# Revit family: Timber-Column
name_source: partatom
category: Structural Columns
revit_build: Autodesk Revit Architecture 2012 (Build: 20110210_1515)
units: mm (PartAtom-declared; Revit-internal decimal feet)

## types (56) — shared parameters
Assembly Code = B10

## per-type parameters (varying)
| type | A | b | d |
| 5x5 | 20.25 in² | 0' - 4 1/2" | 0' - 4 1/2" |
| 6x6 | 30.25 in² | 0' - 5 1/2" | 0' - 5 1/2" |
| 6x8 | 41.25 in² | 0' - 5 1/2" | 0' - 7 1/2" |
| 6x10 | 52.25 in² | 0' - 5 1/2" | 0' - 9 1/2" |
| 6x12 | 63.25 in² | 0' - 5 1/2" | 0' - 11 1/2" |
| 6x14 | 74.25 in² | 0' - 5 1/2" | 1' - 1 1/2" |
| 6x16 | 85.25 in² | 0' - 5 1/2" | 1' - 3 1/2" |
| 6x18 | 96.25 in² | 0' - 5 1/2" | 1' - 5 1/2" |
| 6x20 | 107.3 in² | 0' - 5 1/2" | 1' - 7 1/2" |
| 6x22 | 118.3 in² | 0' - 5 1/2" | 1' - 9 1/2" |
| 6x24 | 129.3 in² | 0' - 5 1/2" | 1' - 11 1/2" |
| 8x8 | 56.25 in² | 0' - 7 1/2" | 0' - 7 1/2" |
| 8x10 | 71.25 in² | 0' - 7 1/2" | 0' - 9 1/2" |
| 8x12 | 86.25 in² | 0' - 7 1/2" | 0' - 11 1/2" |
| 8x14 | 101.3 in² | 0' - 7 1/2" | 1' - 1 1/2" |
| 8x16 | 116.3 in² | 0' - 7 1/2" | 1' - 3 1/2" |
| 8x18 | 131.3 in² | 0' - 7 1/2" | 1' - 5 1/2" |
| 8x20 | 146.3 in² | 0' - 7 1/2" | 1' - 7 1/2" |
| 8x22 | 161.3 in² | 0' - 7 1/2" | 1' - 9 1/2" |
| 8x24 | 176.3 in² | 0' - 7 1/2" | 1' - 11 1/2" |
| 10x10 | 90.25 in² | 0' - 9 1/2" | 0' - 9 1/2" |
| 10x12 | 109.3 in² | 0' - 9 1/2" | 0' - 11 1/2" |
| 10x14 | 128.3 in² | 0' - 9 1/2" | 1' - 1 1/2" |
| 10x16 | 147.3 in² | 0' - 9 1/2" | 1' - 3 1/2" |
| 10x18 | 166.3 in² | 0' - 9 1/2" | 1' - 5 1/2" |
| 10x20 | 185.3 in² | 0' - 9 1/2" | 1' - 7 1/2" |
| 10x22 | 204.3 in² | 0' - 9 1/2" | 1' - 9 1/2" |
| 10x24 | 223.3 in² | 0' - 9 1/2" | 1' - 11 1/2" |
| 12x12 | 132.3 in² | 0' - 11 1/2" | 0' - 11 1/2" |
| 12x14 | 155.3 in² | 0' - 11 1/2" | 1' - 1 1/2" |
| 12x16 | 178.3 in² | 0' - 11 1/2" | 1' - 3 1/2" |
| 12x18 | 201.3 in² | 0' - 11 1/2" | 1' - 5 1/2" |
| 12x20 | 224.3 in² | 0' - 11 1/2" | 1' - 7 1/2" |
| 12x22 | 247.3 in² | 0' - 11 1/2" | 1' - 9 1/2" |
| 12x24 | 270.3 in² | 0' - 11 1/2" | 1' - 11 1/2" |
| 14x14 | 182.3 in² | 1' - 1 1/2" | 1' - 1 1/2" |
| 14x16 | 209.3 in² | 1' - 1 1/2" | 1' - 3 1/2" |
| 14x18 | 236.3 in² | 1' - 1 1/2" | 1' - 5 1/2" |
| 14x20 | 263.3 in² | 1' - 1 1/2" | 1' - 7 1/2" |
| 14x22 | 290.3 in² | 1' - 1 1/2" | 1' - 9 1/2" |
| 14x24 | 317.3 in² | 1' - 1 1/2" | 1' - 11 1/2" |
| 16x16 | 240.3 in² | 1' - 3 1/2" | 1' - 3 1/2" |
| 16x18 | 271.3 in² | 1' - 3 1/2" | 1' - 5 1/2" |
| 16x20 | 302.3 in² | 1' - 3 1/2" | 1' - 7 1/2" |
| 16x22 | 333.3 in² | 1' - 3 1/2" | 1' - 9 1/2" |
| 16x24 | 364.3 in² | 1' - 3 1/2" | 1' - 11 1/2" |
| 18x18 | 306.3 in² | 1' - 5 1/2" | 1' - 5 1/2" |
| 18x20 | 341.3 in² | 1' - 5 1/2" | 1' - 7 1/2" |
| 18x22 | 376.3 in² | 1' - 5 1/2" | 1' - 9 1/2" |
| 18x24 | 411.3 in² | 1' - 5 1/2" | 1' - 11 1/2" |
| 20x20 | 380.3 in² | 1' - 7 1/2" | 1' - 7 1/2" |
| 20x22 | 419.3 in² | 1' - 7 1/2" | 1' - 9 1/2" |
| 20x24 | 458.3 in² | 1' - 7 1/2" | 1' - 11 1/2" |
| 22x22 | 462.3 in² | 1' - 9 1/2" | 1' - 9 1/2" |
| 22x24 | 505.3 in² | 1' - 9 1/2" | 1' - 11 1/2" |
| 24x24 | 552.3 in² | 1' - 11 1/2" | 1' - 11 1/2" |

## geometry (parser evidence)
native form markers: Sweep x1
no freeform markers — native parametric forms only
